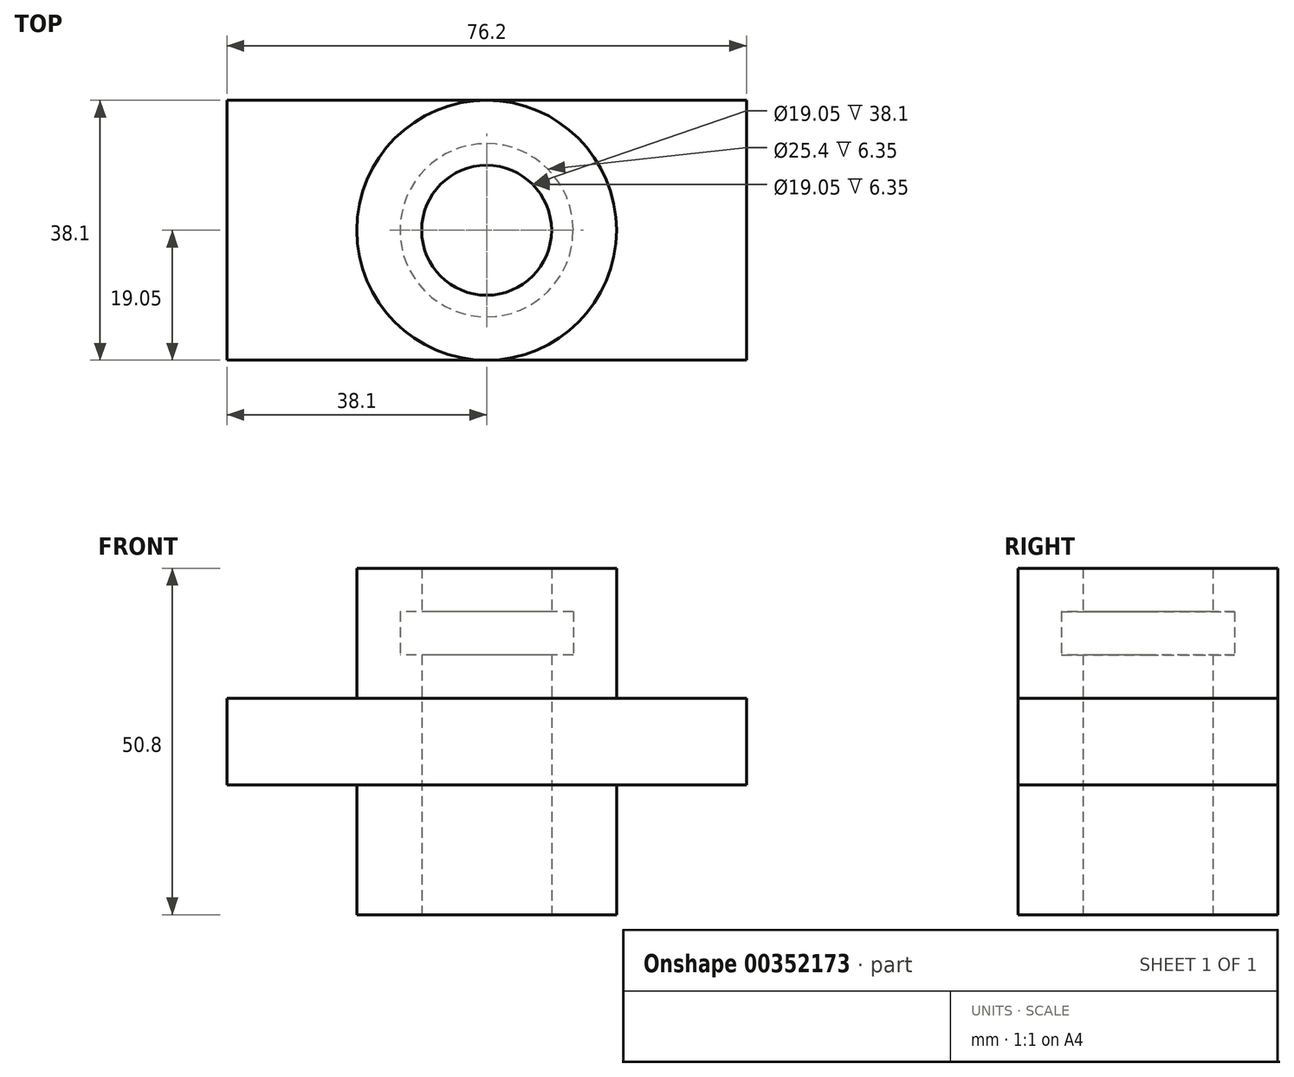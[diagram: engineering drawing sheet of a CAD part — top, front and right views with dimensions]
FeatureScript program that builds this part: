
annotation { "Feature Type Name" : "Feature", "Feature Type Description" : "" }
export const myFeature = defineFeature(function(context is Context, id is Id, definition is map)
    precondition{}
    {
        {
            var Q0;
            Q0=qCreatedBy(makeId("Front.planeOp"),FACE);
            var sketch = newSketch(context, id + "F0", { "sketchPlane" : qUnion([Q0])});
            skLineSegment(sketch, "E0", {"start": v(0, 0) * mm, "end": v(0, 12.7) * mm});
            skLineSegment(sketch, "E1", {"start": v(0, 12.7) * mm, "end": v(76.2, 12.7) * mm});
            skLineSegment(sketch, "E2", {"start": v(76.2, 12.7) * mm, "end": v(76.2, 0) * mm});
            skLineSegment(sketch, "E3", {"start": v(76.2, 0) * mm, "end": v(0, 0) * mm});
            skSolve(sketch);
        }
        {
            var Q0;
            Q0=makeQuery(id+"F0.imprint","IMPRINT",FACE,{"disambiguationData":[TD([[makeQuery(id+"F0.imprint","IMPRINT",EDGE,{"derivedFrom":sQuery(id+"F0.wireOp",EDGE,"E0")}),-1.0]])]});
            extrude(context, id + "F1", {"entities" : qUnion([Q0]), "depth" : 38.1 * mm});
        }
        {
            var Q0;
            Q0=makeQuery(id+"F1.opExtrude","SWEPT_FACE",FACE,{"disambiguationData":[OSD([sQuery(id+"F0.wireOp",EDGE,"E1")])]});
            var sketch = newSketch(context, id + "F2", { "sketchPlane" : qUnion([Q0])});
            skLineSegment(sketch, "E4", {"start": v(0, -19.05) * mm, "end": v(76.2, -19.05) * mm, "construction": true});
            skLineSegment(sketch, "E5", {"start": v(38.1, 0) * mm, "end": v(38.1, -38.1) * mm, "construction": true});
            skCircle(sketch, "E6", {"center": v(38.1, -19.05) * mm, "radius": 19.05 * mm});
            skCircle(sketch, "E7", {"center": v(38.1, -19.05) * mm, "radius": 9.53 * mm});
            skSolve(sketch);
        }
        {
            var Q0;
            Q0=makeQuery(id+"F2.imprint","IMPRINT",FACE,{"disambiguationData":[TD([[makeQuery(id+"F2.imprint","IMPRINT",EDGE,{"derivedFrom":sQuery(id+"F2.wireOp",EDGE,"E7")}),-1.0]])]});
            extrude(context, id + "F3", {"entities" : qUnion([Q0]), "operationType" : NewBodyOperationType.ADD, "depth" : 6.35 * mm});
        }
        {
            var Q0;
            Q0=makeQuery(id+"F3.boolean.opBoolean","SPLIT",FACE,{"disambiguationData":[TD([makeQuery(id+"F3.opExtrude","SWEPT_FACE",FACE,{"disambiguationData":[OSD([sQuery(id+"F2.wireOp",EDGE,"E7")])]})])],"derivedFrom":makeQuery(id+"F1.opExtrude","SWEPT_FACE",FACE,{"disambiguationData":[OSD([sQuery(id+"F0.wireOp",EDGE,"E1")])]})});
            extrude(context, id + "F4", {"entities" : qUnion([Q0]), "operationType" : NewBodyOperationType.REMOVE, "endBound" : BoundingType.THROUGH_ALL, "oppositeDirection" : true, "depth" : 25.4 * mm});
        }
        {
            var Q0;
            Q0=makeQuery(id+"F1.opExtrude","SWEPT_FACE",FACE,{"disambiguationData":[OSD([sQuery(id+"F0.wireOp",EDGE,"E3")])]});
            var sketch = newSketch(context, id + "F5", { "sketchPlane" : qUnion([Q0])});
            skLineSegment(sketch, "E8", {"start": v(0, 19.05) * mm, "end": v(76.2, 19.05) * mm, "construction": true});
            skLineSegment(sketch, "E9", {"start": v(38.1, 38.1) * mm, "end": v(38.1, 0) * mm, "construction": true});
            skCircle(sketch, "E10", {"center": v(38.1, 19.05) * mm, "radius": 19.05 * mm});
            skCircle(sketch, "E11", {"center": v(38.1, 19.05) * mm, "radius": 9.53 * mm});
            skSolve(sketch);
        }
        {
            var Q0;
            Q0=makeQuery(id+"F5.imprint","IMPRINT",FACE,{"disambiguationData":[TD([[makeQuery(id+"F5.imprint","IMPRINT",EDGE,{"derivedFrom":sQuery(id+"F5.wireOp",EDGE,"E11")}),-1.0]])]});
            extrude(context, id + "F6", {"entities" : qUnion([Q0]), "operationType" : NewBodyOperationType.ADD, "depth" : 19.05 * mm});
        }
        {
            var Q0;
            Q0=makeQuery(id+"F3.opExtrude","CAP_FACE",FACE,{"disambiguationData":[OSD([sQuery(id+"F2.wireOp",EDGE,"E6"),sQuery(id+"F2.wireOp",EDGE,"E7")])],"isStart":false});
            var sketch = newSketch(context, id + "F7", { "sketchPlane" : qUnion([Q0])});
            skCircle(sketch, "E12", {"center": v(38.1, -19.05) * mm, "radius": 12.7 * mm});
            skSolve(sketch);
        }
        {
            var Q0;
            Q0=makeQuery(id+"F7.imprint","IMPRINT",FACE,{"disambiguationData":[TD([[makeQuery(id+"F7.imprint","IMPRINT",EDGE,{"derivedFrom":sQuery(id+"F7.wireOp",EDGE,"E12")}),-1.0]])]});
            extrude(context, id + "F8", {"entities" : qUnion([Q0]), "operationType" : NewBodyOperationType.ADD, "depth" : 6.35 * mm});
        }
        {
            var Q0;
            Q0=makeQuery(id+"F8.opExtrude","CAP_FACE",FACE,{"disambiguationData":[OSD([sQuery(id+"F2.wireOp",EDGE,"E6"),sQuery(id+"F7.wireOp",EDGE,"E12")])],"isStart":false});
            var sketch = newSketch(context, id + "F9", { "sketchPlane" : qUnion([Q0])});
            skCircle(sketch, "E13", {"center": v(38.1, -19.05) * mm, "radius": 19.05 * mm});
            skCircle(sketch, "E14", {"center": v(38.1, -19.05) * mm, "radius": 9.53 * mm});
            skSolve(sketch);
        }
        {
            var Q0;
            Q0=makeQuery(id+"F9.imprint","IMPRINT",FACE,{"disambiguationData":[TD([[makeQuery(id+"F9.imprint","IMPRINT",EDGE,{"derivedFrom":sQuery(id+"F9.wireOp",EDGE,"E14")}),-1.0]])]});
            var Q1;
            Q1=makeQuery(id+"F9.imprint","IMPRINT",FACE,{"disambiguationData":[TD([[makeQuery(id+"F9.imprint","IMPRINT",EDGE,{"derivedFrom":sQuery(id+"F9.wireOp",EDGE,"E13")}),1.0]])]});
            extrude(context, id + "F10", {"entities" : qUnion([Q0, Q1]), "operationType" : NewBodyOperationType.ADD, "depth" : 6.35 * mm});
        }
    });
